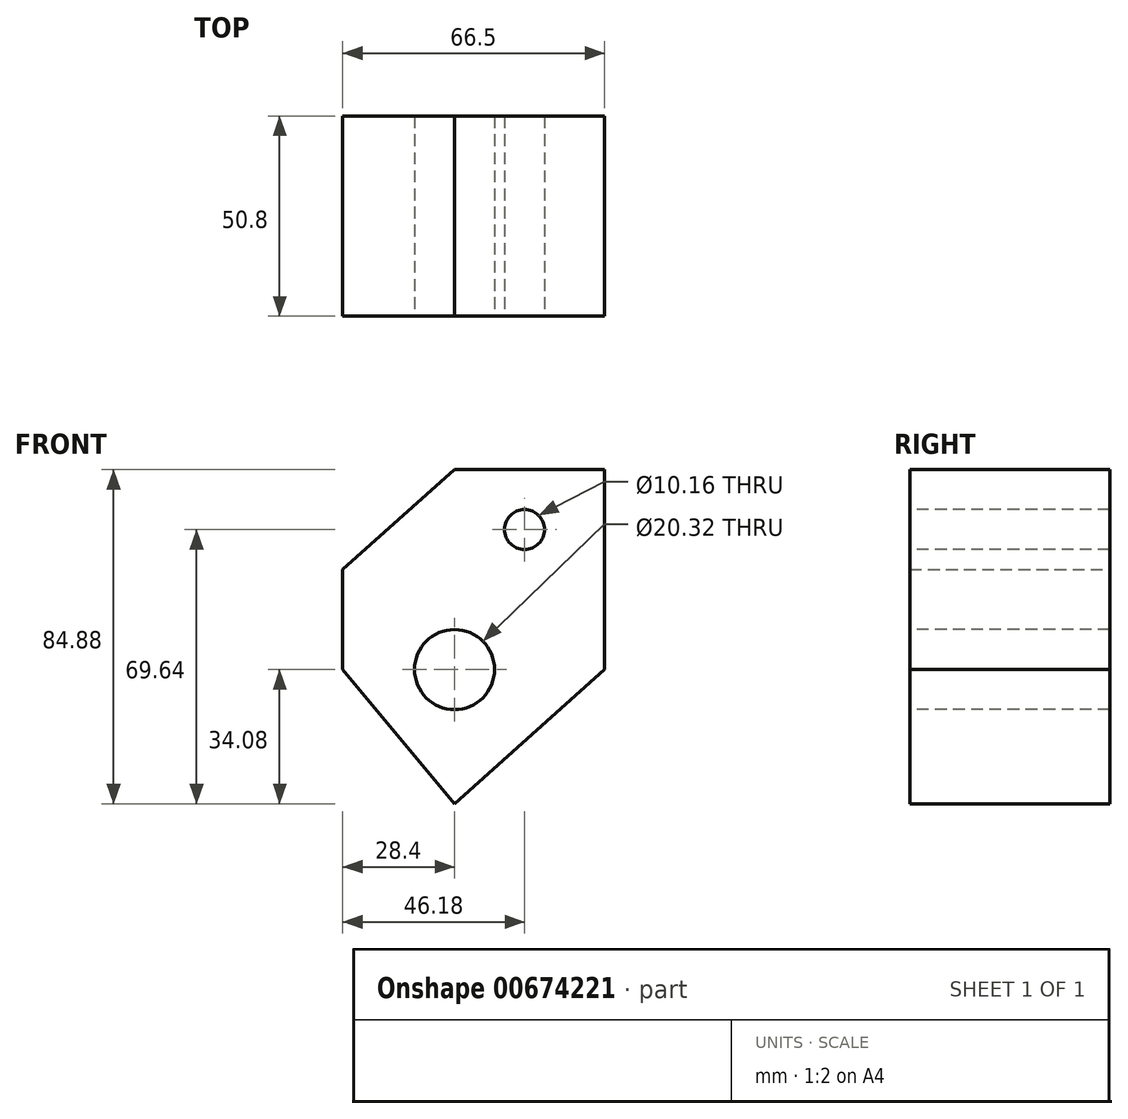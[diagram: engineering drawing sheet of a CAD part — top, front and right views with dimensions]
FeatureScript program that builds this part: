
annotation { "Feature Type Name" : "Feature", "Feature Type Description" : "" }
export const myFeature = defineFeature(function(context is Context, id is Id, definition is map)
    precondition{}
    {
        {
            var Q0;
            Q0=qCreatedBy(makeId("Front.planeOp"),FACE);
            var sketch = newSketch(context, id + "F0", { "sketchPlane" : qUnion([Q0])});
            skLineSegment(sketch, "E0", {"start": v(-28.4, 0) * mm, "end": v(-28.4, 25.4) * mm});
            skLineSegment(sketch, "E1", {"start": v(-28.4, 25.4) * mm, "end": v(0, 50.8) * mm});
            skLineSegment(sketch, "E2", {"start": v(0, 50.8) * mm, "end": v(38.1, 50.8) * mm});
            skLineSegment(sketch, "E3", {"start": v(38.1, 50.8) * mm, "end": v(38.1, 0) * mm});
            skLineSegment(sketch, "E4", {"start": v(38.1, 0) * mm, "end": v(0, -34.08) * mm});
            skLineSegment(sketch, "E5", {"start": v(0, -34.08) * mm, "end": v(-28.4, 0) * mm});
            skSolve(sketch);
        }
        {
            var Q0;
            Q0 = qSketchRegion(id + "F0", true);
            extrude(context, id + "F1", {"entities" : qUnion([Q0]), "depth" : 25.4 * mm, "offsetDistance" : 25.4 * mm, "hasSecondDirection" : true, "secondDirectionOppositeDirection" : true, "secondDirectionDepth" : 25.4 * mm});
        }
        {
            var Q0;
            Q0=makeQuery(id+"F1.opExtrude","CAP_FACE",FACE,{"disambiguationData":[OSD([sQuery(id+"F0.wireOp",EDGE,"E0"),sQuery(id+"F0.wireOp",EDGE,"E1"),sQuery(id+"F0.wireOp",EDGE,"E2"),sQuery(id+"F0.wireOp",EDGE,"E3"),sQuery(id+"F0.wireOp",EDGE,"E4"),sQuery(id+"F0.wireOp",EDGE,"E5")])],"isStart":false});
            var sketch = newSketch(context, id + "F2", { "sketchPlane" : qUnion([Q0])});
            skCircle(sketch, "E6", {"center": v(0, 0) * mm, "radius": 10.16 * mm});
            skCircle(sketch, "E7", {"center": v(17.78, 35.56) * mm, "radius": 5.08 * mm});
            skSolve(sketch);
        }
        {
            var Q0;
            Q0 = qSketchRegion(id + "F2", true);
            extrude(context, id + "F3", {"entities" : qUnion([Q0]), "operationType" : NewBodyOperationType.REMOVE, "endBound" : BoundingType.THROUGH_ALL, "oppositeDirection" : true, "depth" : 25.4 * mm, "offsetDistance" : 25.4 * mm});
        }
    });
